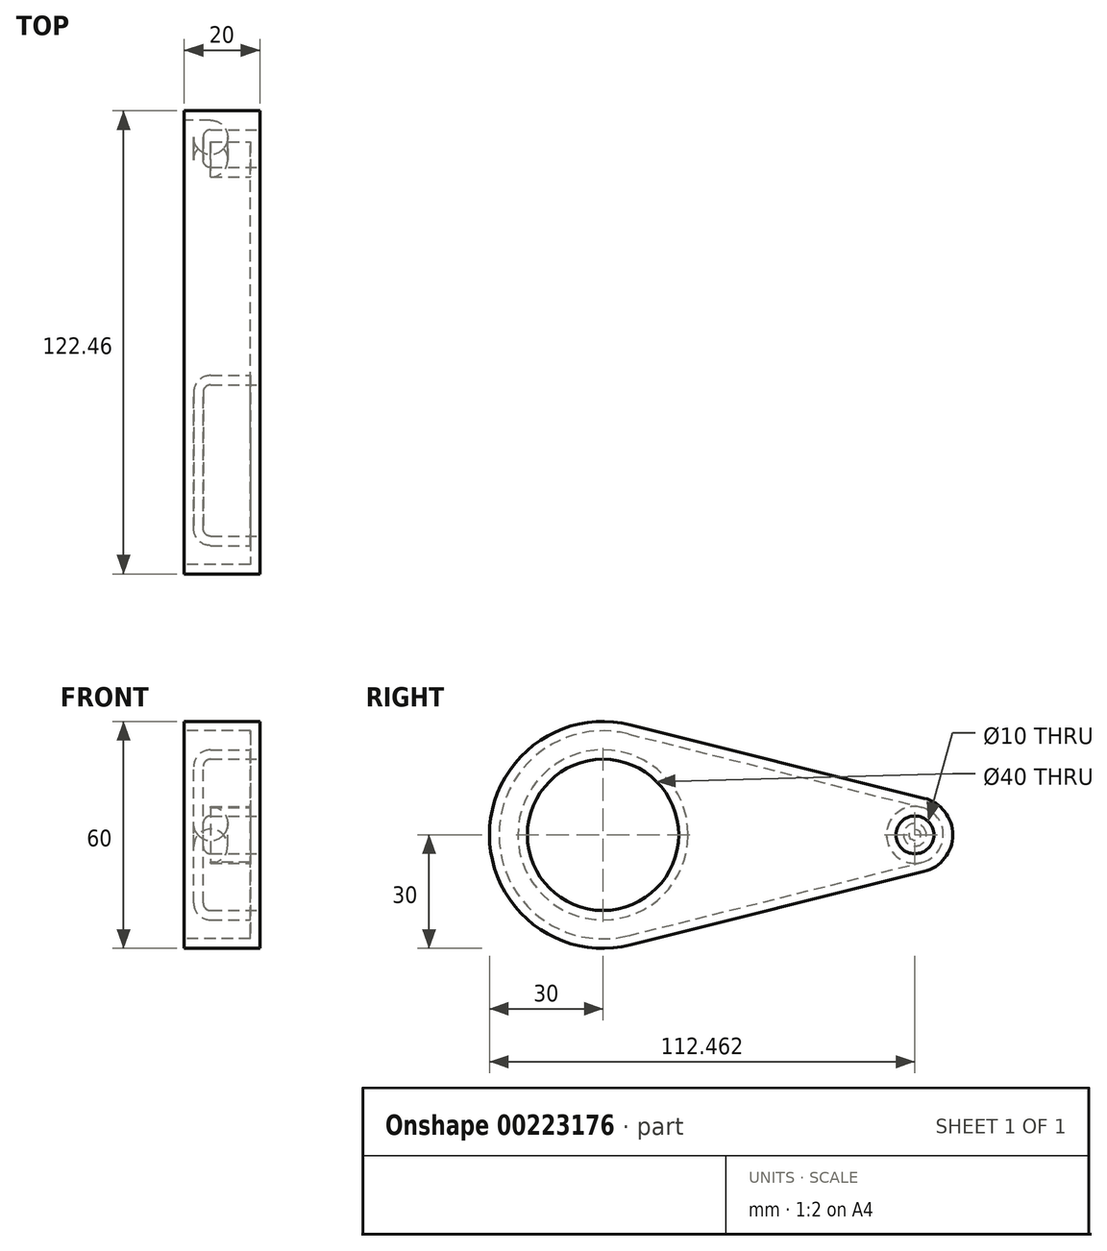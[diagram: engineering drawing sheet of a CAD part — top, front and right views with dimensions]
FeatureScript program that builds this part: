
annotation { "Feature Type Name" : "Feature", "Feature Type Description" : "" }
export const myFeature = defineFeature(function(context is Context, id is Id, definition is map)
    precondition{}
    {
        {
            var Q0;
            Q0=qCreatedBy(makeId("Right.planeOp"),FACE);
            var sketch = newSketch(context, id + "F0", { "sketchPlane" : qUnion([Q0])});
            skCircle(sketch, "E0", {"center": v(0, 0) * mm, "radius": 30 * mm});
            skCircle(sketch, "E1", {"center": v(82.46, 0) * mm, "radius": 10 * mm});
            skLineSegment(sketch, "E2", {"start": v(7.28, 29.1) * mm, "end": v(84.89, 9.7) * mm});
            skLineSegment(sketch, "E3", {"start": v(7.28, -29.1) * mm, "end": v(84.89, -9.7) * mm});
            skSolve(sketch);
        }
        {
            var Q0;
            {var subQ0=sQuery(id+"F0.wireOp",EDGE,"E1");var subQ1=makeQuery(id+"F0.imprint","INTERSECT",VERTEX,{"derivedFrom":[subQ0,sQuery(id+"F0.wireOp",EDGE,"E2")]});Q0=makeQuery(id+"F0.imprint","IMPRINT",FACE,{"disambiguationData":[TD([[makeQuery(id+"F0.imprint","IMPRINT",EDGE,{"disambiguationData":[TD([[subQ1,-1.0]])],"derivedFrom":subQ0}),1.0]])]});}
            var Q1;
            {var subQ0=sQuery(id+"F0.wireOp",EDGE,"E2");Q1=makeQuery(id+"F0.imprint","IMPRINT",FACE,{"disambiguationData":[TD([[makeQuery(id+"F0.imprint","IMPRINT",EDGE,{"derivedFrom":subQ0}),-1.0]])]});}
            var Q2;
            {var subQ0=sQuery(id+"F0.wireOp",EDGE,"E0");var subQ1=makeQuery(id+"F0.imprint","INTERSECT",VERTEX,{"derivedFrom":[subQ0,sQuery(id+"F0.wireOp",EDGE,"E2")]});Q2=makeQuery(id+"F0.imprint","IMPRINT",FACE,{"disambiguationData":[TD([[makeQuery(id+"F0.imprint","IMPRINT",EDGE,{"disambiguationData":[TD([[subQ1,-1.0]])],"derivedFrom":subQ0}),1.0]])]});}
            extrude(context, id + "F1", {"entities" : qUnion([Q0, Q1, Q2]), "depth" : 20 * mm});
        }
        {
            var Q0;
            Q0=makeQuery(id+"F1.opExtrude","CAP_FACE",FACE,{"disambiguationData":[OSD([sQuery(id+"F0.wireOp",EDGE,"E0"),sQuery(id+"F0.wireOp",EDGE,"E1"),sQuery(id+"F0.wireOp",EDGE,"E2"),sQuery(id+"F0.wireOp",EDGE,"E3")])],"isStart":false});
            var sketch = newSketch(context, id + "F2", { "sketchPlane" : qUnion([Q0])});
            skCircle(sketch, "E4", {"center": v(0, 0) * mm, "radius": 20 * mm});
            skCircle(sketch, "E5", {"center": v(82.46, 0) * mm, "radius": 5 * mm});
            skSolve(sketch);
        }
        {
            var Q0;
            Q0=makeQuery(id+"F2.imprint","IMPRINT",FACE,{"disambiguationData":[TD([[makeQuery(id+"F2.imprint","IMPRINT",EDGE,{"derivedFrom":sQuery(id+"F2.wireOp",EDGE,"E4")}),1.0]])]});
            var Q1;
            Q1=makeQuery(id+"F2.imprint","IMPRINT",FACE,{"disambiguationData":[TD([[makeQuery(id+"F2.imprint","IMPRINT",EDGE,{"derivedFrom":sQuery(id+"F2.wireOp",EDGE,"E5")}),1.0]])]});
            extrude(context, id + "F3", {"entities" : qUnion([Q0, Q1]), "operationType" : NewBodyOperationType.REMOVE, "oppositeDirection" : true, "depth" : 15 * mm});
        }
        {
            var Q0;
            Q0=makeQuery(id+"F3.boolean.opBoolean","COPY",EDGE,{"derivedFrom":makeQuery(id+"F3.opExtrude","CAP_EDGE",EDGE,{"disambiguationData":[OSD([sQuery(id+"F2.wireOp",EDGE,"E4")])],"isStart":false})});
            var Q1;
            Q1=makeQuery(id+"F3.boolean.opBoolean","COPY",EDGE,{"derivedFrom":makeQuery(id+"F3.opExtrude","CAP_EDGE",EDGE,{"disambiguationData":[OSD([sQuery(id+"F2.wireOp",EDGE,"E4")])],"isStart":true})});
            var Q2;
            Q2=makeQuery(id+"F3.boolean.opBoolean","COPY",EDGE,{"derivedFrom":makeQuery(id+"F3.opExtrude","CAP_EDGE",EDGE,{"disambiguationData":[OSD([sQuery(id+"F2.wireOp",EDGE,"E5")])],"isStart":true})});
            var Q3;
            Q3=makeQuery(id+"F3.boolean.opBoolean","COPY",EDGE,{"derivedFrom":makeQuery(id+"F3.opExtrude","CAP_EDGE",EDGE,{"disambiguationData":[OSD([sQuery(id+"F2.wireOp",EDGE,"E5")])],"isStart":false})});
            fillet(context, id + "F4", {"entities" : qUnion([Q0, Q1, Q2, Q3]), "radius" : 2 * mm, "tangentPropagation" : true, "allowEdgeOverflow" : false});
        }
        {
            var Q0;
            Q0=makeQuery(id+"F1.opExtrude","CAP_FACE",FACE,{"disambiguationData":[OSD([sQuery(id+"F0.wireOp",EDGE,"E0"),sQuery(id+"F0.wireOp",EDGE,"E1"),sQuery(id+"F0.wireOp",EDGE,"E2"),sQuery(id+"F0.wireOp",EDGE,"E3")])],"isStart":true});
            shell(context, id + "F5", {"entities" : qUnion([Q0]), "thickness" : 2.5 * mm});
        }
    });
